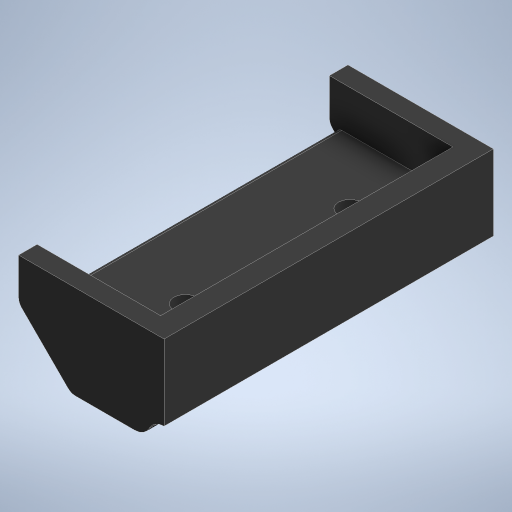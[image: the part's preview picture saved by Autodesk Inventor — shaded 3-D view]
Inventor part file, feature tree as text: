
AUTODESK INVENTOR PART (.ipt)
format: ipt  version: 2024 (Build 280153000, 153)  size: 278,528 bytes
history: native  units: in
note: dims shown in document units (in); Inventor stores cm internally (conversion verified against a paired STEP export)
features: extrude x4, sketch x4, fillet x3, projected_geometry x2
ambient origin geometry x8: Origin, YZ Plane, XZ Plane, XY Plane, X Axis, Y Axis, Z Axis, Center Point
bodies: Solid1 (feature_tree)
feature tree (13):
  extrude  "Extrusion1"  Depth=0.44in
  extrude  "Extrusion2"  Depth=8.0in TaperAngle=0.0deg
  extrude  "Extrusion3"  Depth=0.4in
  extrude  "Extrusion4"  Depth=0.25in
  fillet  "Fillet1"  Radius=0.22in
  fillet  "Fillet2"  Radius=8.0in
  fillet  "Fillet3"  Radius=3.0in
  sketch  "Sketch1"  dims[d1=0.44in d2=0.44in]
  sketch  "Sketch2"  dims[d3=0.4in d4=8.0in d5=0.0in]
  sketch  "Sketch3"  dims[d6=2.7in d7=0.4in]
  projected_geometry  "Projected Loop1"
  sketch  "Sketch4"  dims[d9=1.8in d11=0.22in d12=0.22in d13=8.0in d14=0.0in d15=3.0in d16=3.55in d17=7.1in d18=1.0in d19=0.0in d20=0.55in d21=0.55in d22=0.75in d23=0.0in d24=0.125in d25=0.25in d26=0.25in]
  projected_geometry  "Projected Loop2"
